# Revit family: result
name_source: partatom
category: Generic Models
revit_build: Autodesk Revit 2015 (Build: 20140903_1530(x64)
units: mm (PartAtom-declared; Revit-internal decimal feet)

## types (1)
- Default
    Brand url = http://www.gessi.it
    Design country = Italy
    Edition number = 1
    IFC Classification = Furnishing Element
    Installation instructions = https://www.gessi.com
    Manufacturer country = Italy
    Manufacturer name = Gessi
    Material main = Steel
    Material secondary = Steel
    Product Guid = 1408c289-993b-4f77-bd27-782635383488
    Product SKU = 59549
    Product certification = https://www.gessi.com
    Product data url = https://bimobject.com
    Product family = RILIEVO
    Product group = RILIEVO ACCESSORI
    Product name = 20VENTI - Shelf 30 cm - 59549
    Product url = https://www.gessi.com
    QR code = http://bimobject.com
    Uniclass 2015 Code = Pr_30_36_59_38
    Uniclass 2015 Name = Holders and hooks

## geometry (parser evidence)
native form markers: Sweep x4
no freeform markers — native parametric forms only
